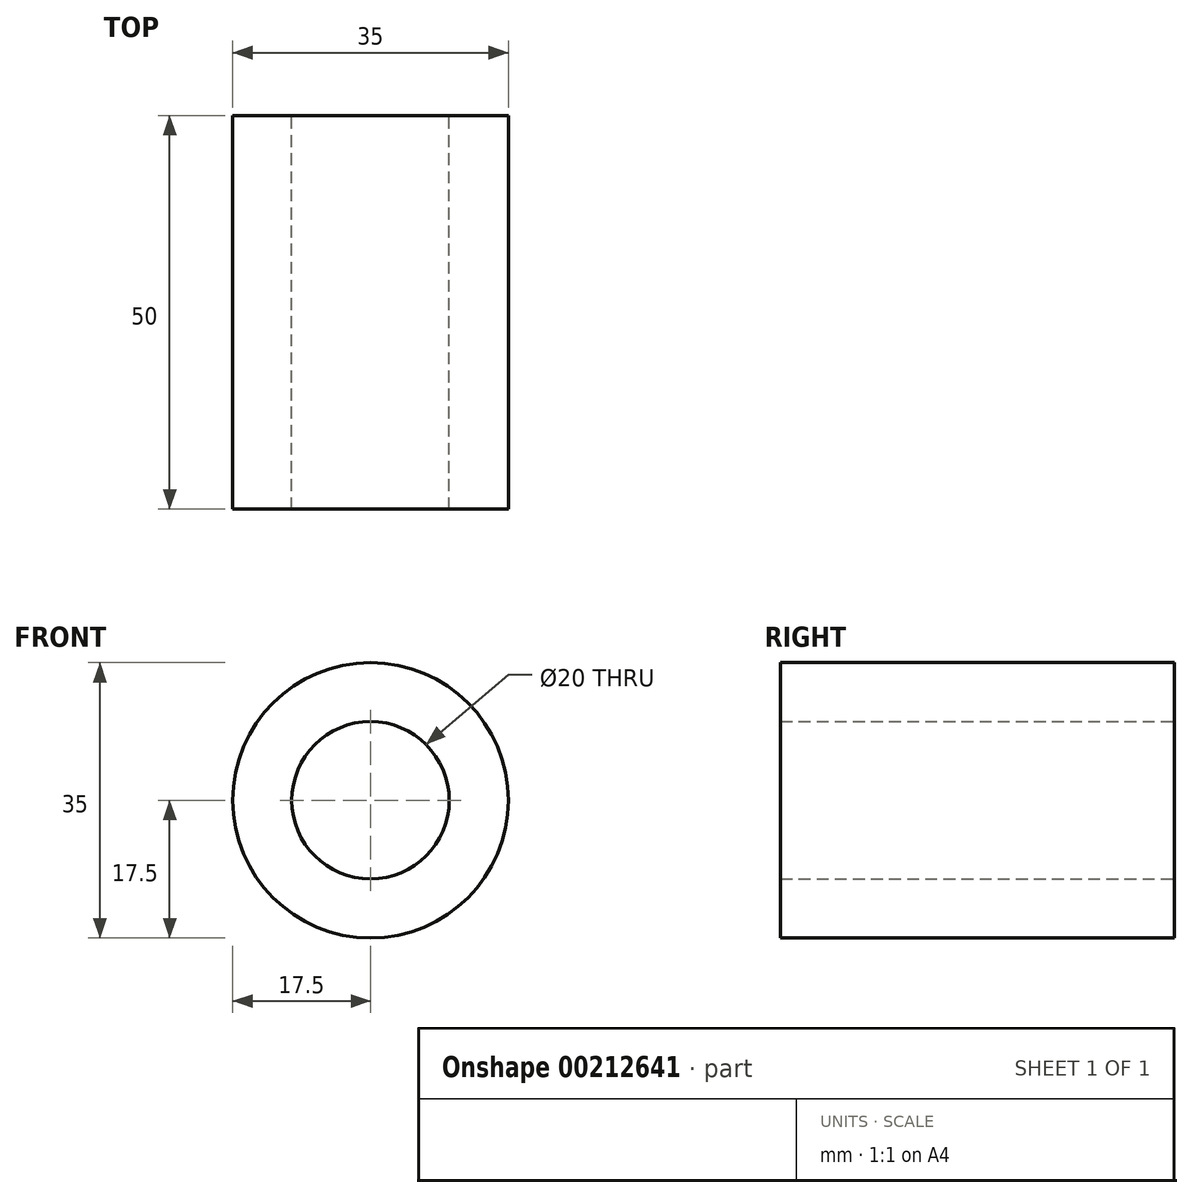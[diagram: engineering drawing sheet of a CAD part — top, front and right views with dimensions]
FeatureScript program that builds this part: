
annotation { "Feature Type Name" : "Feature", "Feature Type Description" : "" }
export const myFeature = defineFeature(function(context is Context, id is Id, definition is map)
    precondition{}
    {
        {
            var Q0;
            Q0=qCreatedBy(makeId("Front.planeOp"),FACE);
            var sketch = newSketch(context, id + "F0", { "sketchPlane" : qUnion([Q0])});
            skCircle(sketch, "E0", {"center": v(0, 0) * mm, "radius": 17.5 * mm});
            skCircle(sketch, "E1", {"center": v(0, 0) * mm, "radius": 10 * mm});
            skSolve(sketch);
        }
        {
            var Q0;
            Q0 = qSketchRegion(id + "F0", true);
            extrude(context, id + "F1", {"entities" : qUnion([Q0]), "depth" : 50 * mm});
        }
    });
